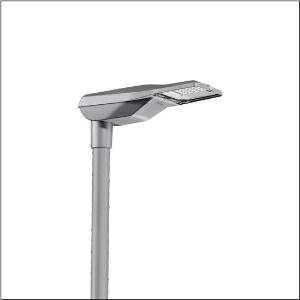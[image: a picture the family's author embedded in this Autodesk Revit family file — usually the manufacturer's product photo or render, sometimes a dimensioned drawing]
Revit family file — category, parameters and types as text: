
# Revit family: streetlight_sl_21_iq_micro___st1_0ab_5xe1m31d08cb_a4c0
name_source: partatom
category: Lighting Fixtures
units: mm (PartAtom-declared; Revit-internal decimal feet)

## family parameters
Cut with Voids When Loaded = No
Host = Face
Light Source = No
Part Type = Normal
Room Calculation Point = No
Round Connector Dimension = Use Diameter
Shared = No

## types (1)
- --- (1 x LED, 2520 lm, 19.4 W, 3000K)
    Apparent Load = 19 VA
    CIE Flux Codes = 38 73 97 100 100
    Color Rendering = 70
    Color Temperature = 3000K
    Default Elevation = 1800 mm
    Description = Streetlight SL 21 iQ micro, mast luminaire, primary light control with lens, of PMMA, primary optical cover: cover, of toughened safety glass, transparent, light distribution: ST1.0aB, light emission: direct distribution, primary light characteristic: asymmetric, installation type: post-top, side-entry, LED, High Power LED, rated luminous flux: 2.520lm, luminous efficacy: 130lm/W, light colour: 730, colour temperature: 3000K, control: Auto-Match, Temp-Guard, Lumen-Switch, Night-Set, Smart-Wire, Light-Fading, Desk-Remote (wireless, voltage-free reading and setting of iQ features in the workshop via application-optimized NFC function/RFID function), optimised constant luminous flux control (CLO 2.0), pre-setting: linear dimming characteristic, mains connection: 220..240V, AC, 50/60Hz, start of lifetime: 19W, end of service life: 20W, reduction: 10W, luminaire housing, of diecast aluminium, powder-coated, Siteco® metallic grey (DB 702S), corrosivity category C5 mid according to DIN EN ISO 12944, please order mast flange separately, inclination adjustable: 0°, 5°, 10°, 15°, sealing non-destructively replaceable, multi-level sealing system, length: 528mm, width: 235mm, height: 110mm, mast flange for spigot size: 42mm (side-entry): 5XC10008XM4, 60/48mm (side-entry/post-top): 5XC10108XM2, 76/60mm (side-entry/post-top): 5XC10108XM1, protection rating (complete): IP66, insulation class (complete): insulation class II (safety insulation), certification: CE, ENEC, ENEC+, VDE, impact resistance: IK09, permissible operating ambient temperature for outdoor applications: -40..+50°C, standard-compliant lighting for roads and squares, packaging unit: 1 piece

Light Distribution: ST1.0aB
    Height = 110 mm
    Lamp = 1 x LED
    Lamp Light Flux = 2520 lm
    Lamp Power = 19.4 W
    Lamp count = 1
    Length = 528 mm
    Luminous efficacy = 130 lm/W
    Manufacturer = Siteco
    ModVariant = No
    Model = 5XE1M31D08CB
    Number of Poles = 1
    OnlyDefault = Yes
    Power Factor = 1
    Product Name = Streetlight SL 21 iQ micro | ST1.0aB
    Product group = mast luminaire | pylon top
    ProductGroupID = 6100
    Protection Class = Protection class II
    Protection Degree = IP 66
    RLX_Detail_Level = 1
    RLX_Emergency_Light_Flux = 0 lm
    RLX_Emergency_Type = 0
    RLX_Emergency_Type_DB = No
    RlxData = <blob elided: 98697 chars, md5=170271c0>
    Socket = socket
    Standby Power = 0 W
    System Light Flux = 2520 lm
    System Power = 19 W
    Type Comments = factory setting: luminous flux: 100 % | dim-lin: 254 | 387 mA
    Type Image = l_1006881.jpg
    URL = http://relux.com
    VarID = @adj_107983
    Voltage = 0 V
    Weight = 0.00 kg
    Width = 235 mm

## geometry (parser evidence)
native form markers: Blend x4, Sweep x11
no freeform markers — native parametric forms only
